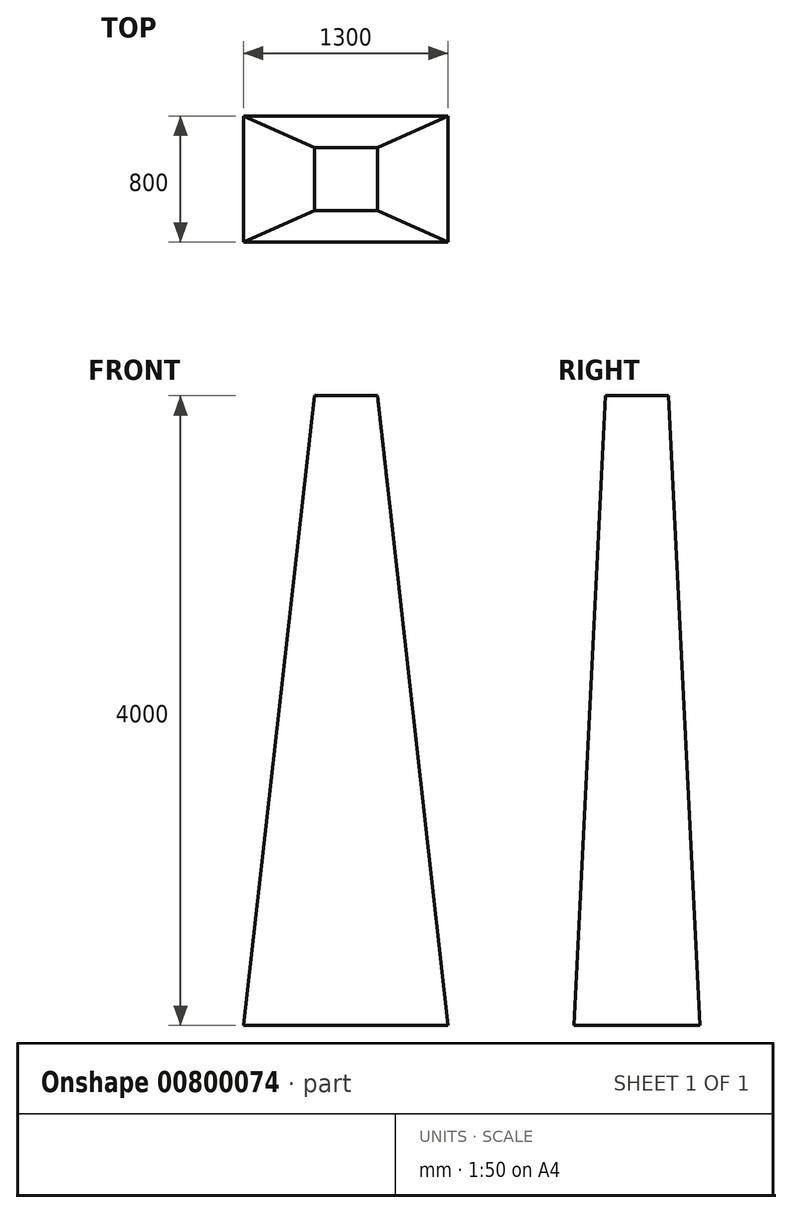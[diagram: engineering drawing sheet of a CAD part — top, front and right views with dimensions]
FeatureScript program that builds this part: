
annotation { "Feature Type Name" : "Feature", "Feature Type Description" : "" }
export const myFeature = defineFeature(function(context is Context, id is Id, definition is map)
    precondition{}
    {
        {
            var Q0;
            Q0=qCreatedBy(makeId("Top.planeOp"),FACE);
            var sketch = newSketch(context, id + "F0", { "sketchPlane" : qUnion([Q0])});
            skLineSegment(sketch, "E0.bottom", {"start": v(650, -400) * mm, "end": v(-650, -400) * mm});
            skLineSegment(sketch, "E0.top", {"start": v(650, 400) * mm, "end": v(-650, 400) * mm});
            skLineSegment(sketch, "E0.left", {"start": v(650, -400) * mm, "end": v(650, 400) * mm});
            skLineSegment(sketch, "E0.right", {"start": v(-650, -400) * mm, "end": v(-650, 400) * mm});
            skPoint(sketch, "E0.middle", {"position": v(0, 0) * mm});
            skSolve(sketch);
        }
        {
            var Q0;
            Q0=makeQuery(id+"F0.imprint","IMPRINT",FACE,{"disambiguationData":[TD([[makeQuery(id+"F0.imprint","IMPRINT",EDGE,{"derivedFrom":sQuery(id+"F0.wireOp",EDGE,"E0.bottom")}),-1.0]])]});
            cPlane(context, id + "F1", {"entities" : qUnion([Q0]), "cplaneType" : CPlaneType.OFFSET, "offset" : 4000 * mm, "width" : 150 * mm, "height" : 150 * mm});
        }
        {
            var Q0;
            Q0=qCreatedBy(id+"F1.planeOp",FACE);
            var sketch = newSketch(context, id + "F2", { "sketchPlane" : qUnion([Q0])});
            skLineSegment(sketch, "E1.bottom", {"start": v(200, -200) * mm, "end": v(-200, -200) * mm});
            skLineSegment(sketch, "E1.top", {"start": v(200, 200) * mm, "end": v(-200, 200) * mm});
            skLineSegment(sketch, "E1.left", {"start": v(200, -200) * mm, "end": v(200, 200) * mm});
            skLineSegment(sketch, "E1.right", {"start": v(-200, -200) * mm, "end": v(-200, 200) * mm});
            skPoint(sketch, "E1.middle", {"position": v(0, 0) * mm});
            skSolve(sketch);
        }
        {
            var Q0;
            Q0=makeQuery(id+"F2.imprint","IMPRINT",FACE,{"disambiguationData":[TD([[makeQuery(id+"F2.imprint","IMPRINT",EDGE,{"derivedFrom":sQuery(id+"F2.wireOp",EDGE,"E1.bottom")}),-1.0]])]});
            var Q1;
            Q1=makeQuery(id+"F0.imprint","IMPRINT",FACE,{"disambiguationData":[TD([[makeQuery(id+"F0.imprint","IMPRINT",EDGE,{"derivedFrom":sQuery(id+"F0.wireOp",EDGE,"E0.bottom")}),-1.0]])]});
            loft(context, id + "F3", {"sheetProfilesArray" : [{ "sheetProfileEntities" : qUnion([Q0]) }, { "sheetProfileEntities" : qUnion([Q1]) }]});
        }
        {
            var Q0;
            Q0=makeQuery(id+"F3.opLoft","CAP_FACE",FACE,{"disambiguationData":[OSD([makeQuery(id+"F0.imprint","IMPRINT",FACE,{"disambiguationData":[TD([[makeQuery(id+"F0.imprint","IMPRINT",EDGE,{"derivedFrom":sQuery(id+"F0.wireOp",EDGE,"E0.bottom")}),-1.0]])]})])],"isStart":true});
            shell(context, id + "F4", {"entities" : qUnion([Q0]), "thickness" : 2.5 * mm});
        }
    });
